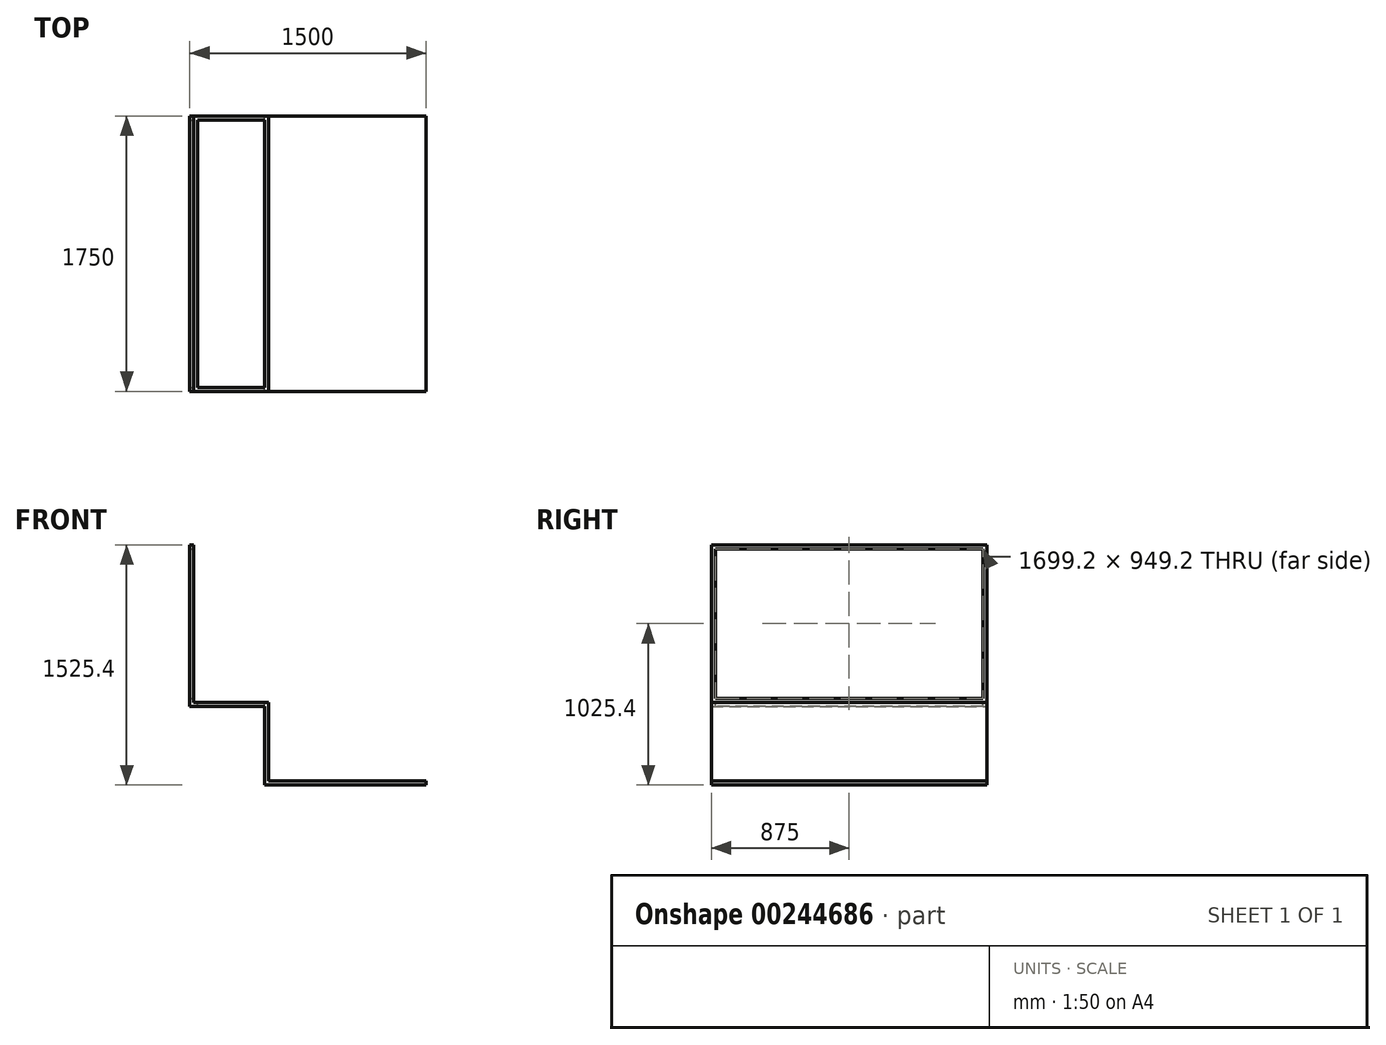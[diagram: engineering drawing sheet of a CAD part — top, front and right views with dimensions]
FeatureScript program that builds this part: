
annotation { "Feature Type Name" : "Feature", "Feature Type Description" : "" }
export const myFeature = defineFeature(function(context is Context, id is Id, definition is map)
    precondition{}
    {
        {
            var Q0;
            Q0=qCreatedBy(makeId("Front.planeOp"),FACE);
            var sketch = newSketch(context, id + "F0", { "sketchPlane" : qUnion([Q0])});
            skLineSegment(sketch, "E0", {"start": v(0, 0) * mm, "end": v(0, 500) * mm});
            skLineSegment(sketch, "E1", {"start": v(0, 500) * mm, "end": v(-500, 500) * mm});
            skLineSegment(sketch, "E2", {"start": v(0, 0) * mm, "end": v(1000, 0) * mm});
            skLineSegment(sketch, "E3", {"start": v(-500, 500) * mm, "end": v(-500, 474.6) * mm});
            skLineSegment(sketch, "E4", {"start": v(-500, 474.6) * mm, "end": v(-25.4, 474.6) * mm});
            skLineSegment(sketch, "E5", {"start": v(-25.4, 474.6) * mm, "end": v(-25.4, -25.4) * mm});
            skLineSegment(sketch, "E6", {"start": v(-25.4, -25.4) * mm, "end": v(1000, -25.4) * mm});
            skLineSegment(sketch, "E7", {"start": v(1000, -25.4) * mm, "end": v(1000, 0) * mm});
            skLineSegment(sketch, "E8.bottom", {"start": v(-500, 474.6) * mm, "end": v(-474.6, 474.6) * mm});
            skLineSegment(sketch, "E8.top", {"start": v(-500, 1500) * mm, "end": v(-474.6, 1500) * mm});
            skLineSegment(sketch, "E8.left", {"start": v(-500, 474.6) * mm, "end": v(-500, 1500) * mm});
            skLineSegment(sketch, "E8.right", {"start": v(-474.6, 474.6) * mm, "end": v(-474.6, 1500) * mm});
            skSolve(sketch);
        }
        {
            var Q0;
            Q0 = qSketchRegion(id + "F0", true);
            extrude(context, id + "F1", {"entities" : qUnion([Q0]), "depth" : 1750 * mm});
        }
        {
            var Q0;
            Q0=makeQuery(id+"F1.opExtrude","SWEPT_FACE",FACE,{"disambiguationData":[OSD([sQuery(id+"F0.wireOp",EDGE,"E1")])]});
            var sketch = newSketch(context, id + "F2", { "sketchPlane" : qUnion([Q0])});
            skLineSegment(sketch, "E9.bottom", {"start": v(-449.2, -25.4) * mm, "end": v(-25.4, -25.4) * mm});
            skLineSegment(sketch, "E9.top", {"start": v(-449.2, -1724.6) * mm, "end": v(-25.4, -1724.6) * mm});
            skLineSegment(sketch, "E9.left", {"start": v(-449.2, -25.4) * mm, "end": v(-449.2, -1724.6) * mm});
            skLineSegment(sketch, "E9.right", {"start": v(-25.4, -25.4) * mm, "end": v(-25.4, -1724.6) * mm});
            skSolve(sketch);
        }
        {
            var Q0;
            Q0=makeQuery(id+"F2.imprint","IMPRINT",FACE,{"disambiguationData":[TD([[makeQuery(id+"F2.imprint","IMPRINT",EDGE,{"derivedFrom":sQuery(id+"F2.wireOp",EDGE,"E9.bottom")}),-1.0]])]});
            extrude(context, id + "F3", {"entities" : qUnion([Q0]), "operationType" : NewBodyOperationType.REMOVE, "oppositeDirection" : true, "depth" : 25.4 * mm});
        }
        {
            var Q0;
            Q0=makeQuery(id+"F1.opExtrude","SWEPT_FACE",FACE,{"disambiguationData":[OSD([sQuery(id+"F0.wireOp",EDGE,"E8.right")])]});
            var sketch = newSketch(context, id + "F4", { "sketchPlane" : qUnion([Q0])});
            skLineSegment(sketch, "E10.bottom", {"start": v(-1724.6, 1474.6) * mm, "end": v(-25.4, 1474.6) * mm});
            skLineSegment(sketch, "E10.top", {"start": v(-1724.6, 525.4) * mm, "end": v(-25.4, 525.4) * mm});
            skLineSegment(sketch, "E10.left", {"start": v(-1724.6, 1474.6) * mm, "end": v(-1724.6, 525.4) * mm});
            skLineSegment(sketch, "E10.right", {"start": v(-25.4, 1474.6) * mm, "end": v(-25.4, 525.4) * mm});
            skSolve(sketch);
        }
        {
            var Q0;
            Q0=makeQuery(id+"F4.imprint","IMPRINT",FACE,{"disambiguationData":[TD([[makeQuery(id+"F4.imprint","IMPRINT",EDGE,{"derivedFrom":sQuery(id+"F4.wireOp",EDGE,"E10.bottom")}),-1.0]])]});
            extrude(context, id + "F5", {"entities" : qUnion([Q0]), "operationType" : NewBodyOperationType.REMOVE, "oppositeDirection" : true, "depth" : 25.4 * mm});
        }
    });
